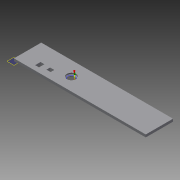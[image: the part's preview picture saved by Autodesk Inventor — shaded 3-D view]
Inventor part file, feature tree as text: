
AUTODESK INVENTOR PART (.ipt)
format: ipt  version: 2015 SP1 (Build 190203100, 203)  size: 247,296 bytes
history: native  units: mm
features: sketch x1, plane x1, extrude x1, hole x1
ambient origin geometry x8: Origin, YZ Plane, XZ Plane, XY Plane, X Axis, Y Axis, Z Axis, Center Point
bodies: Body1 (feature_tree)
feature tree (4):
  sketch  "Sketch1"  dims[d0=415.0mm d1=86.0mm d2=82.0mm d3=54.0mm d4=13.0mm d5=11.5mm d8=18.0mm d9=12.0mm d10=17.0mm d11=54.0mm d12=22.0mm d13=45.0mm d14=45.0mm d15=8.0mm d16=0.0mm d17=10.0mm d18=10.0mm d19=29.0mm d20=6.0mm d21=4.0mm d22=2.0mm d23=90.0deg d24=4.0mm d25=20.594885mm]
  plane  "Work Plane1"
  extrude  "Extrusion2"  Depth=86.0mm
  hole  "Hole1"  [1 undecoded]
note: 1 required parameter value undecoded (feature->parameter linkage not recoverable at this tier; creation-order binding heuristic only, values carry confidence <= 0.55)
